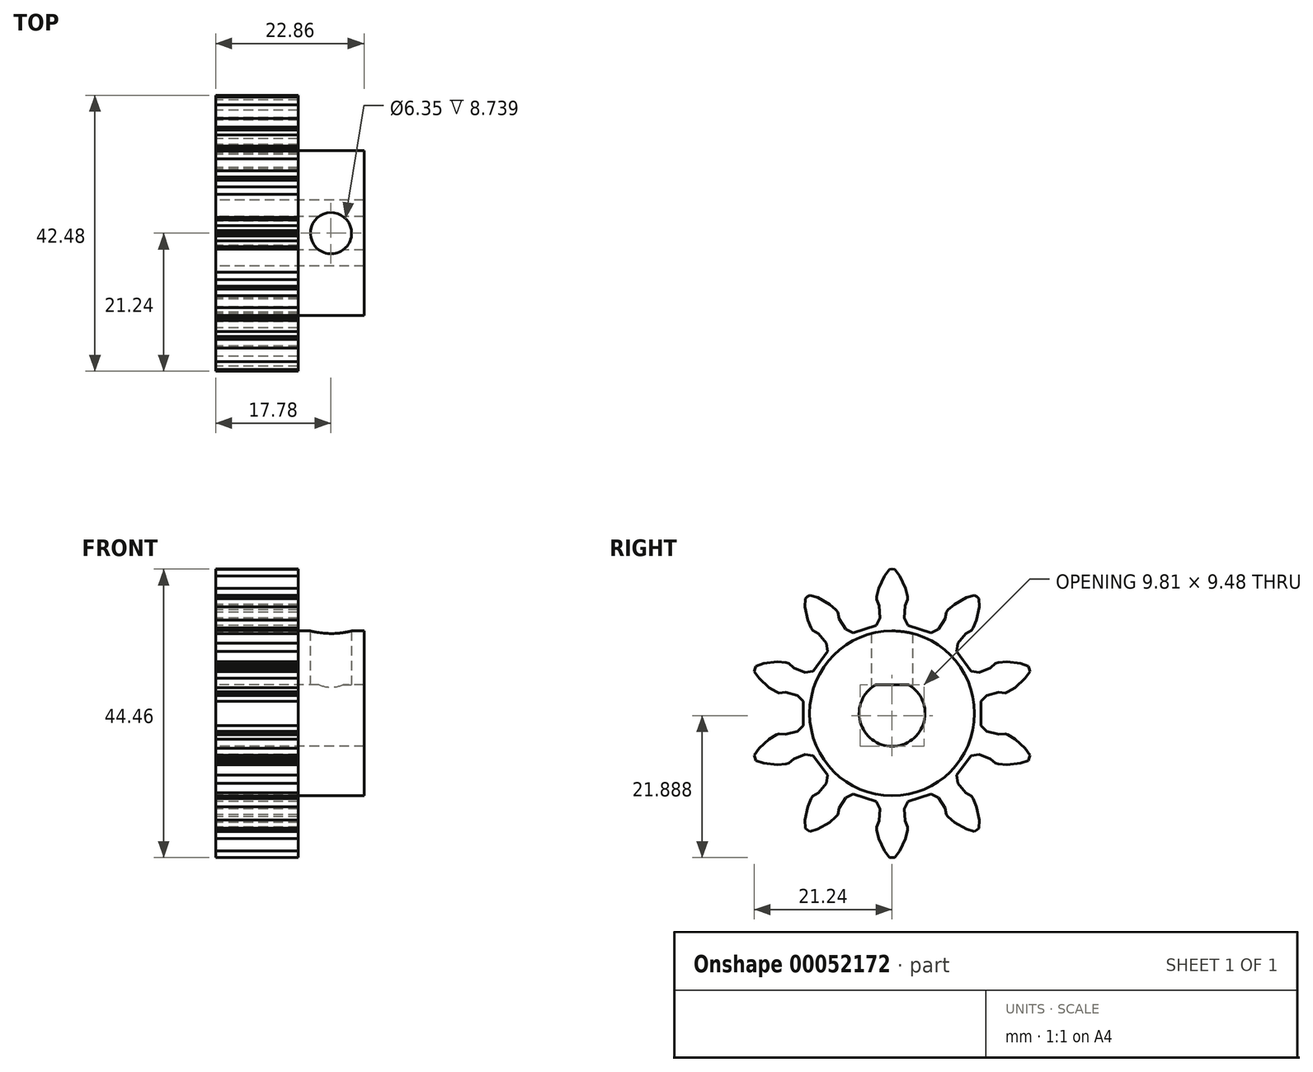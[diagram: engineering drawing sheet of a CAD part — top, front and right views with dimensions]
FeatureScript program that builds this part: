
annotation { "Feature Type Name" : "Feature", "Feature Type Description" : "" }
export const myFeature = defineFeature(function(context is Context, id is Id, definition is map)
    precondition{}
    {
        {
            var Q0;
            Q0=qCreatedBy(makeId("Right.planeOp"),FACE);
            var sketch = newSketch(context, id + "F0", { "sketchPlane" : qUnion([Q0])});
            skLineSegment(sketch, "E0", {"start": v(-20.97, 7.27) * mm, "end": v(-21.14, 6.87) * mm});
            skLineSegment(sketch, "E1", {"start": v(-21.14, 6.87) * mm, "end": v(-21.24, 6.44) * mm});
            skLineSegment(sketch, "E2", {"start": v(-21.24, 6.44) * mm, "end": v(-20.5, 5.4) * mm});
            skLineSegment(sketch, "E3", {"start": v(-20.5, 5.4) * mm, "end": v(-18.97, 3.97) * mm});
            skLineSegment(sketch, "E4", {"start": v(-18.97, 3.97) * mm, "end": v(-17.83, 3.3) * mm});
            skLineSegment(sketch, "E5", {"start": v(-17.83, 3.3) * mm, "end": v(-17.4, 3.15) * mm});
            skLineSegment(sketch, "E6", {"start": v(-17.4, 3.15) * mm, "end": v(-16.39, 3.24) * mm});
            skLineSegment(sketch, "E7", {"start": v(-16.39, 3.24) * mm, "end": v(-14.55, 2.78) * mm});
            skLineSegment(sketch, "E8", {"start": v(-14.55, 2.78) * mm, "end": v(-13.65, 1.86) * mm});
            skLineSegment(sketch, "E9", {"start": v(-13.65, 1.86) * mm, "end": v(-13.65, -1.86) * mm});
            skLineSegment(sketch, "E10", {"start": v(-13.65, -1.86) * mm, "end": v(-14.55, -2.78) * mm});
            skLineSegment(sketch, "E11", {"start": v(-14.55, -2.78) * mm, "end": v(-16.39, -3.24) * mm});
            skLineSegment(sketch, "E12", {"start": v(-16.39, -3.24) * mm, "end": v(-17.4, -3.15) * mm});
            skLineSegment(sketch, "E13", {"start": v(-17.4, -3.15) * mm, "end": v(-17.83, -3.3) * mm});
            skLineSegment(sketch, "E14", {"start": v(-17.83, -3.3) * mm, "end": v(-18.97, -3.97) * mm});
            skLineSegment(sketch, "E15", {"start": v(-18.97, -3.97) * mm, "end": v(-20.5, -5.4) * mm});
            skLineSegment(sketch, "E16", {"start": v(-20.5, -5.4) * mm, "end": v(-21.24, -6.44) * mm});
            skLineSegment(sketch, "E17", {"start": v(-21.24, -6.44) * mm, "end": v(-21.14, -6.87) * mm});
            skLineSegment(sketch, "E18", {"start": v(-21.14, -6.87) * mm, "end": v(-20.97, -7.27) * mm});
            skLineSegment(sketch, "E19", {"start": v(-20.97, -7.27) * mm, "end": v(-19.77, -7.68) * mm});
            skLineSegment(sketch, "E20", {"start": v(-19.77, -7.68) * mm, "end": v(-17.68, -7.93) * mm});
            skLineSegment(sketch, "E21", {"start": v(-17.68, -7.93) * mm, "end": v(-16.36, -7.82) * mm});
            skLineSegment(sketch, "E22", {"start": v(-16.36, -7.82) * mm, "end": v(-15.93, -7.68) * mm});
            skLineSegment(sketch, "E23", {"start": v(-15.93, -7.68) * mm, "end": v(-15.16, -7.01) * mm});
            skLineSegment(sketch, "E24", {"start": v(-15.16, -7.01) * mm, "end": v(-13.4, -6.3) * mm});
            skLineSegment(sketch, "E25", {"start": v(-13.4, -6.3) * mm, "end": v(-12.14, -6.52) * mm});
            skLineSegment(sketch, "E26", {"start": v(-12.14, -6.52) * mm, "end": v(-9.95, -9.53) * mm});
            skLineSegment(sketch, "E27", {"start": v(-9.95, -9.53) * mm, "end": v(-10.14, -10.8) * mm});
            skLineSegment(sketch, "E28", {"start": v(-10.14, -10.8) * mm, "end": v(-11.35, -12.25) * mm});
            skLineSegment(sketch, "E29", {"start": v(-11.35, -12.25) * mm, "end": v(-12.23, -12.77) * mm});
            skLineSegment(sketch, "E30", {"start": v(-12.23, -12.77) * mm, "end": v(-12.49, -13.14) * mm});
            skLineSegment(sketch, "E31", {"start": v(-12.49, -13.14) * mm, "end": v(-13, -14.36) * mm});
            skLineSegment(sketch, "E32", {"start": v(-13, -14.36) * mm, "end": v(-13.41, -16.43) * mm});
            skLineSegment(sketch, "E33", {"start": v(-13.41, -16.43) * mm, "end": v(-13.4, -17.7) * mm});
            skLineSegment(sketch, "E34", {"start": v(-13.4, -17.7) * mm, "end": v(-13.06, -17.98) * mm});
            skLineSegment(sketch, "E35", {"start": v(-13.06, -17.98) * mm, "end": v(-12.7, -18.2) * mm});
            skLineSegment(sketch, "E36", {"start": v(-12.7, -18.2) * mm, "end": v(-11.48, -17.83) * mm});
            skLineSegment(sketch, "E37", {"start": v(-11.48, -17.83) * mm, "end": v(-9.64, -16.81) * mm});
            skLineSegment(sketch, "E38", {"start": v(-9.64, -16.81) * mm, "end": v(-8.64, -15.94) * mm});
            skLineSegment(sketch, "E39", {"start": v(-8.64, -15.94) * mm, "end": v(-8.37, -15.58) * mm});
            skLineSegment(sketch, "E40", {"start": v(-8.37, -15.58) * mm, "end": v(-8.14, -14.58) * mm});
            skLineSegment(sketch, "E41", {"start": v(-8.14, -14.58) * mm, "end": v(-7.14, -12.98) * mm});
            skLineSegment(sketch, "E42", {"start": v(-7.14, -12.98) * mm, "end": v(-6, -12.4) * mm});
            skLineSegment(sketch, "E43", {"start": v(-6, -12.4) * mm, "end": v(-2.45, -13.56) * mm});
            skLineSegment(sketch, "E44", {"start": v(-2.45, -13.56) * mm, "end": v(-1.85, -14.7) * mm});
            skLineSegment(sketch, "E45", {"start": v(-1.85, -14.7) * mm, "end": v(-1.99, -16.58) * mm});
            skLineSegment(sketch, "E46", {"start": v(-1.99, -16.58) * mm, "end": v(-2.39, -17.52) * mm});
            skLineSegment(sketch, "E47", {"start": v(-2.39, -17.52) * mm, "end": v(-2.38, -17.97) * mm});
            skLineSegment(sketch, "E48", {"start": v(-2.38, -17.97) * mm, "end": v(-2.08, -19.27) * mm});
            skLineSegment(sketch, "E49", {"start": v(-2.08, -19.27) * mm, "end": v(-1.2, -21.17) * mm});
            skLineSegment(sketch, "E50", {"start": v(-1.2, -21.17) * mm, "end": v(-0.43, -22.2) * mm});
            skLineSegment(sketch, "E51", {"start": v(-0.43, -22.2) * mm, "end": v(0, -22.23) * mm});
            skLineSegment(sketch, "E52", {"start": v(0, -22.23) * mm, "end": v(0.43, -22.2) * mm});
            skLineSegment(sketch, "E53", {"start": v(0.43, -22.2) * mm, "end": v(1.2, -21.17) * mm});
            skLineSegment(sketch, "E54", {"start": v(1.2, -21.17) * mm, "end": v(2.08, -19.27) * mm});
            skLineSegment(sketch, "E55", {"start": v(2.08, -19.27) * mm, "end": v(2.38, -17.97) * mm});
            skLineSegment(sketch, "E56", {"start": v(2.38, -17.97) * mm, "end": v(2.39, -17.52) * mm});
            skLineSegment(sketch, "E57", {"start": v(2.39, -17.52) * mm, "end": v(1.99, -16.58) * mm});
            skLineSegment(sketch, "E58", {"start": v(1.99, -16.58) * mm, "end": v(1.85, -14.7) * mm});
            skLineSegment(sketch, "E59", {"start": v(1.85, -14.7) * mm, "end": v(2.45, -13.56) * mm});
            skLineSegment(sketch, "E60", {"start": v(2.45, -13.56) * mm, "end": v(6, -12.4) * mm});
            skLineSegment(sketch, "E61", {"start": v(6, -12.4) * mm, "end": v(7.14, -12.98) * mm});
            skLineSegment(sketch, "E62", {"start": v(7.14, -12.98) * mm, "end": v(8.14, -14.58) * mm});
            skLineSegment(sketch, "E63", {"start": v(8.14, -14.58) * mm, "end": v(8.37, -15.58) * mm});
            skLineSegment(sketch, "E64", {"start": v(8.37, -15.58) * mm, "end": v(8.64, -15.94) * mm});
            skLineSegment(sketch, "E65", {"start": v(8.64, -15.94) * mm, "end": v(9.64, -16.81) * mm});
            skLineSegment(sketch, "E66", {"start": v(9.64, -16.81) * mm, "end": v(11.48, -17.83) * mm});
            skLineSegment(sketch, "E67", {"start": v(11.48, -17.83) * mm, "end": v(12.7, -18.2) * mm});
            skLineSegment(sketch, "E68", {"start": v(12.7, -18.2) * mm, "end": v(13.06, -17.98) * mm});
            skLineSegment(sketch, "E69", {"start": v(13.06, -17.98) * mm, "end": v(13.4, -17.7) * mm});
            skLineSegment(sketch, "E70", {"start": v(13.4, -17.7) * mm, "end": v(13.41, -16.43) * mm});
            skLineSegment(sketch, "E71", {"start": v(13.41, -16.43) * mm, "end": v(13, -14.36) * mm});
            skLineSegment(sketch, "E72", {"start": v(13, -14.36) * mm, "end": v(12.49, -13.14) * mm});
            skLineSegment(sketch, "E73", {"start": v(12.49, -13.14) * mm, "end": v(12.23, -12.77) * mm});
            skLineSegment(sketch, "E74", {"start": v(12.23, -12.77) * mm, "end": v(11.35, -12.25) * mm});
            skLineSegment(sketch, "E75", {"start": v(11.35, -12.25) * mm, "end": v(10.14, -10.8) * mm});
            skLineSegment(sketch, "E76", {"start": v(10.14, -10.8) * mm, "end": v(9.95, -9.53) * mm});
            skLineSegment(sketch, "E77", {"start": v(9.95, -9.53) * mm, "end": v(12.14, -6.52) * mm});
            skLineSegment(sketch, "E78", {"start": v(12.14, -6.52) * mm, "end": v(13.4, -6.3) * mm});
            skLineSegment(sketch, "E79", {"start": v(13.4, -6.3) * mm, "end": v(15.16, -7.01) * mm});
            skLineSegment(sketch, "E80", {"start": v(15.16, -7.01) * mm, "end": v(15.93, -7.68) * mm});
            skLineSegment(sketch, "E81", {"start": v(15.93, -7.68) * mm, "end": v(16.36, -7.82) * mm});
            skLineSegment(sketch, "E82", {"start": v(16.36, -7.82) * mm, "end": v(17.68, -7.93) * mm});
            skLineSegment(sketch, "E83", {"start": v(17.68, -7.93) * mm, "end": v(19.77, -7.68) * mm});
            skLineSegment(sketch, "E84", {"start": v(19.77, -7.68) * mm, "end": v(20.97, -7.27) * mm});
            skLineSegment(sketch, "E85", {"start": v(20.97, -7.27) * mm, "end": v(21.14, -6.87) * mm});
            skLineSegment(sketch, "E86", {"start": v(21.14, -6.87) * mm, "end": v(21.24, -6.44) * mm});
            skLineSegment(sketch, "E87", {"start": v(21.24, -6.44) * mm, "end": v(20.5, -5.4) * mm});
            skLineSegment(sketch, "E88", {"start": v(20.5, -5.4) * mm, "end": v(18.97, -3.97) * mm});
            skLineSegment(sketch, "E89", {"start": v(18.97, -3.97) * mm, "end": v(17.83, -3.3) * mm});
            skLineSegment(sketch, "E90", {"start": v(17.83, -3.3) * mm, "end": v(17.4, -3.15) * mm});
            skLineSegment(sketch, "E91", {"start": v(17.4, -3.15) * mm, "end": v(16.39, -3.24) * mm});
            skLineSegment(sketch, "E92", {"start": v(16.39, -3.24) * mm, "end": v(14.55, -2.78) * mm});
            skLineSegment(sketch, "E93", {"start": v(14.55, -2.78) * mm, "end": v(13.65, -1.86) * mm});
            skLineSegment(sketch, "E94", {"start": v(13.65, -1.86) * mm, "end": v(13.65, 1.86) * mm});
            skLineSegment(sketch, "E95", {"start": v(13.65, 1.86) * mm, "end": v(14.55, 2.78) * mm});
            skLineSegment(sketch, "E96", {"start": v(14.55, 2.78) * mm, "end": v(16.39, 3.24) * mm});
            skLineSegment(sketch, "E97", {"start": v(16.39, 3.24) * mm, "end": v(17.4, 3.15) * mm});
            skLineSegment(sketch, "E98", {"start": v(17.4, 3.15) * mm, "end": v(17.83, 3.3) * mm});
            skLineSegment(sketch, "E99", {"start": v(17.83, 3.3) * mm, "end": v(18.97, 3.97) * mm});
            skLineSegment(sketch, "E100", {"start": v(18.97, 3.97) * mm, "end": v(20.5, 5.4) * mm});
            skLineSegment(sketch, "E101", {"start": v(20.5, 5.4) * mm, "end": v(21.24, 6.44) * mm});
            skLineSegment(sketch, "E102", {"start": v(21.24, 6.44) * mm, "end": v(21.14, 6.87) * mm});
            skLineSegment(sketch, "E103", {"start": v(21.14, 6.87) * mm, "end": v(20.97, 7.27) * mm});
            skLineSegment(sketch, "E104", {"start": v(20.97, 7.27) * mm, "end": v(19.77, 7.68) * mm});
            skLineSegment(sketch, "E105", {"start": v(19.77, 7.68) * mm, "end": v(17.68, 7.93) * mm});
            skLineSegment(sketch, "E106", {"start": v(17.68, 7.93) * mm, "end": v(16.36, 7.82) * mm});
            skLineSegment(sketch, "E107", {"start": v(16.36, 7.82) * mm, "end": v(15.93, 7.68) * mm});
            skLineSegment(sketch, "E108", {"start": v(15.93, 7.68) * mm, "end": v(15.16, 7.01) * mm});
            skLineSegment(sketch, "E109", {"start": v(15.16, 7.01) * mm, "end": v(13.4, 6.3) * mm});
            skLineSegment(sketch, "E110", {"start": v(13.4, 6.3) * mm, "end": v(12.14, 6.52) * mm});
            skLineSegment(sketch, "E111", {"start": v(12.14, 6.52) * mm, "end": v(9.95, 9.53) * mm});
            skLineSegment(sketch, "E112", {"start": v(9.95, 9.53) * mm, "end": v(10.14, 10.8) * mm});
            skLineSegment(sketch, "E113", {"start": v(10.14, 10.8) * mm, "end": v(11.35, 12.25) * mm});
            skLineSegment(sketch, "E114", {"start": v(11.35, 12.25) * mm, "end": v(12.23, 12.77) * mm});
            skLineSegment(sketch, "E115", {"start": v(12.23, 12.77) * mm, "end": v(12.49, 13.14) * mm});
            skLineSegment(sketch, "E116", {"start": v(12.49, 13.14) * mm, "end": v(13, 14.36) * mm});
            skLineSegment(sketch, "E117", {"start": v(13, 14.36) * mm, "end": v(13.41, 16.43) * mm});
            skLineSegment(sketch, "E118", {"start": v(13.41, 16.43) * mm, "end": v(13.4, 17.7) * mm});
            skLineSegment(sketch, "E119", {"start": v(13.4, 17.7) * mm, "end": v(13.06, 17.98) * mm});
            skLineSegment(sketch, "E120", {"start": v(13.06, 17.98) * mm, "end": v(12.7, 18.2) * mm});
            skLineSegment(sketch, "E121", {"start": v(12.7, 18.2) * mm, "end": v(11.48, 17.83) * mm});
            skLineSegment(sketch, "E122", {"start": v(11.48, 17.83) * mm, "end": v(9.64, 16.81) * mm});
            skLineSegment(sketch, "E123", {"start": v(9.64, 16.81) * mm, "end": v(8.64, 15.94) * mm});
            skLineSegment(sketch, "E124", {"start": v(8.64, 15.94) * mm, "end": v(8.37, 15.58) * mm});
            skLineSegment(sketch, "E125", {"start": v(8.37, 15.58) * mm, "end": v(8.14, 14.58) * mm});
            skLineSegment(sketch, "E126", {"start": v(8.14, 14.58) * mm, "end": v(7.14, 12.98) * mm});
            skLineSegment(sketch, "E127", {"start": v(7.14, 12.98) * mm, "end": v(6, 12.4) * mm});
            skLineSegment(sketch, "E128", {"start": v(6, 12.4) * mm, "end": v(2.45, 13.56) * mm});
            skLineSegment(sketch, "E129", {"start": v(2.45, 13.56) * mm, "end": v(1.85, 14.7) * mm});
            skLineSegment(sketch, "E130", {"start": v(1.85, 14.7) * mm, "end": v(1.99, 16.58) * mm});
            skLineSegment(sketch, "E131", {"start": v(1.99, 16.58) * mm, "end": v(2.39, 17.52) * mm});
            skLineSegment(sketch, "E132", {"start": v(2.39, 17.52) * mm, "end": v(2.38, 17.97) * mm});
            skLineSegment(sketch, "E133", {"start": v(2.38, 17.97) * mm, "end": v(2.08, 19.27) * mm});
            skLineSegment(sketch, "E134", {"start": v(2.08, 19.27) * mm, "end": v(1.2, 21.17) * mm});
            skLineSegment(sketch, "E135", {"start": v(1.2, 21.17) * mm, "end": v(0.43, 22.2) * mm});
            skLineSegment(sketch, "E136", {"start": v(0.43, 22.2) * mm, "end": v(0, 22.23) * mm});
            skLineSegment(sketch, "E137", {"start": v(0, 22.23) * mm, "end": v(-0.43, 22.2) * mm});
            skLineSegment(sketch, "E138", {"start": v(-0.43, 22.2) * mm, "end": v(-1.2, 21.17) * mm});
            skLineSegment(sketch, "E139", {"start": v(-1.2, 21.17) * mm, "end": v(-2.08, 19.27) * mm});
            skLineSegment(sketch, "E140", {"start": v(-2.08, 19.27) * mm, "end": v(-2.38, 17.97) * mm});
            skLineSegment(sketch, "E141", {"start": v(-2.38, 17.97) * mm, "end": v(-2.39, 17.52) * mm});
            skLineSegment(sketch, "E142", {"start": v(-2.39, 17.52) * mm, "end": v(-1.99, 16.58) * mm});
            skLineSegment(sketch, "E143", {"start": v(-1.99, 16.58) * mm, "end": v(-1.85, 14.7) * mm});
            skLineSegment(sketch, "E144", {"start": v(-1.85, 14.7) * mm, "end": v(-2.45, 13.56) * mm});
            skLineSegment(sketch, "E145", {"start": v(-2.45, 13.56) * mm, "end": v(-6, 12.4) * mm});
            skLineSegment(sketch, "E146", {"start": v(-6, 12.4) * mm, "end": v(-7.14, 12.98) * mm});
            skLineSegment(sketch, "E147", {"start": v(-7.14, 12.98) * mm, "end": v(-8.14, 14.58) * mm});
            skLineSegment(sketch, "E148", {"start": v(-8.14, 14.58) * mm, "end": v(-8.37, 15.58) * mm});
            skLineSegment(sketch, "E149", {"start": v(-8.37, 15.58) * mm, "end": v(-8.64, 15.94) * mm});
            skLineSegment(sketch, "E150", {"start": v(-8.64, 15.94) * mm, "end": v(-9.64, 16.81) * mm});
            skLineSegment(sketch, "E151", {"start": v(-9.64, 16.81) * mm, "end": v(-11.48, 17.83) * mm});
            skLineSegment(sketch, "E152", {"start": v(-11.48, 17.83) * mm, "end": v(-12.7, 18.2) * mm});
            skLineSegment(sketch, "E153", {"start": v(-12.7, 18.2) * mm, "end": v(-13.06, 17.98) * mm});
            skLineSegment(sketch, "E154", {"start": v(-13.06, 17.98) * mm, "end": v(-13.4, 17.7) * mm});
            skLineSegment(sketch, "E155", {"start": v(-13.4, 17.7) * mm, "end": v(-13.41, 16.43) * mm});
            skLineSegment(sketch, "E156", {"start": v(-13.41, 16.43) * mm, "end": v(-13, 14.36) * mm});
            skLineSegment(sketch, "E157", {"start": v(-13, 14.36) * mm, "end": v(-12.49, 13.14) * mm});
            skLineSegment(sketch, "E158", {"start": v(-12.49, 13.14) * mm, "end": v(-12.23, 12.77) * mm});
            skLineSegment(sketch, "E159", {"start": v(-12.23, 12.77) * mm, "end": v(-11.35, 12.25) * mm});
            skLineSegment(sketch, "E160", {"start": v(-11.35, 12.25) * mm, "end": v(-10.14, 10.8) * mm});
            skLineSegment(sketch, "E161", {"start": v(-10.14, 10.8) * mm, "end": v(-9.95, 9.53) * mm});
            skLineSegment(sketch, "E162", {"start": v(-9.95, 9.53) * mm, "end": v(-12.14, 6.52) * mm});
            skLineSegment(sketch, "E163", {"start": v(-12.14, 6.52) * mm, "end": v(-13.4, 6.3) * mm});
            skLineSegment(sketch, "E164", {"start": v(-13.4, 6.3) * mm, "end": v(-15.16, 7.01) * mm});
            skLineSegment(sketch, "E165", {"start": v(-15.16, 7.01) * mm, "end": v(-15.93, 7.68) * mm});
            skLineSegment(sketch, "E166", {"start": v(-15.93, 7.68) * mm, "end": v(-16.36, 7.82) * mm});
            skLineSegment(sketch, "E167", {"start": v(-16.36, 7.82) * mm, "end": v(-17.68, 7.93) * mm});
            skLineSegment(sketch, "E168", {"start": v(-17.68, 7.93) * mm, "end": v(-19.77, 7.68) * mm});
            skLineSegment(sketch, "E169", {"start": v(-19.77, 7.68) * mm, "end": v(-20.97, 7.27) * mm});
            skArc(sketch, "E170", {"start": v(-2.55, 4.4) * mm, "mid": v(0, -5.08) * mm, "end": v(2.55, 4.4) * mm});
            skLineSegment(sketch, "E171", {"start": v(-2.55, 4.4) * mm, "end": v(2.55, 4.4) * mm});
            skSolve(sketch);
        }
        {
            var Q0;
            Q0=makeQuery(id+"F0.imprint","IMPRINT",FACE,{"disambiguationData":[TD([[makeQuery(id+"F0.imprint","IMPRINT",EDGE,{"derivedFrom":sQuery(id+"F0.wireOp",EDGE,"E0")}),1.0]])]});
            extrude(context, id + "F1", {"entities" : qUnion([Q0]), "endBound" : BoundingType.SYMMETRIC, "depth" : 12.7 * mm});
        }
        {
            var Q0;
            Q0=makeQuery(id+"F1.opExtrude","CAP_FACE",FACE,{"disambiguationData":[OSD([sQuery(id+"F0.wireOp",EDGE,"E0"),sQuery(id+"F0.wireOp",EDGE,"E1"),sQuery(id+"F0.wireOp",EDGE,"E2"),sQuery(id+"F0.wireOp",EDGE,"E3"),sQuery(id+"F0.wireOp",EDGE,"E4"),sQuery(id+"F0.wireOp",EDGE,"E5"),sQuery(id+"F0.wireOp",EDGE,"E6"),sQuery(id+"F0.wireOp",EDGE,"E7"),sQuery(id+"F0.wireOp",EDGE,"E8"),sQuery(id+"F0.wireOp",EDGE,"E9"),sQuery(id+"F0.wireOp",EDGE,"E10"),sQuery(id+"F0.wireOp",EDGE,"E11"),sQuery(id+"F0.wireOp",EDGE,"E12"),sQuery(id+"F0.wireOp",EDGE,"E13"),sQuery(id+"F0.wireOp",EDGE,"E14"),sQuery(id+"F0.wireOp",EDGE,"E15"),sQuery(id+"F0.wireOp",EDGE,"E16"),sQuery(id+"F0.wireOp",EDGE,"E17"),sQuery(id+"F0.wireOp",EDGE,"E18"),sQuery(id+"F0.wireOp",EDGE,"E19"),sQuery(id+"F0.wireOp",EDGE,"E20"),sQuery(id+"F0.wireOp",EDGE,"E21"),sQuery(id+"F0.wireOp",EDGE,"E22"),sQuery(id+"F0.wireOp",EDGE,"E23"),sQuery(id+"F0.wireOp",EDGE,"E24"),sQuery(id+"F0.wireOp",EDGE,"E25"),sQuery(id+"F0.wireOp",EDGE,"E26"),sQuery(id+"F0.wireOp",EDGE,"E27"),sQuery(id+"F0.wireOp",EDGE,"E28"),sQuery(id+"F0.wireOp",EDGE,"E29"),sQuery(id+"F0.wireOp",EDGE,"E30"),sQuery(id+"F0.wireOp",EDGE,"E31"),sQuery(id+"F0.wireOp",EDGE,"E32"),sQuery(id+"F0.wireOp",EDGE,"E33"),sQuery(id+"F0.wireOp",EDGE,"E34"),sQuery(id+"F0.wireOp",EDGE,"E35"),sQuery(id+"F0.wireOp",EDGE,"E36"),sQuery(id+"F0.wireOp",EDGE,"E37"),sQuery(id+"F0.wireOp",EDGE,"E38"),sQuery(id+"F0.wireOp",EDGE,"E39"),sQuery(id+"F0.wireOp",EDGE,"E40"),sQuery(id+"F0.wireOp",EDGE,"E41"),sQuery(id+"F0.wireOp",EDGE,"E42"),sQuery(id+"F0.wireOp",EDGE,"E43"),sQuery(id+"F0.wireOp",EDGE,"E44"),sQuery(id+"F0.wireOp",EDGE,"E45"),sQuery(id+"F0.wireOp",EDGE,"E46"),sQuery(id+"F0.wireOp",EDGE,"E47"),sQuery(id+"F0.wireOp",EDGE,"E48"),sQuery(id+"F0.wireOp",EDGE,"E49"),sQuery(id+"F0.wireOp",EDGE,"E50"),sQuery(id+"F0.wireOp",EDGE,"E51"),sQuery(id+"F0.wireOp",EDGE,"E52"),sQuery(id+"F0.wireOp",EDGE,"E53"),sQuery(id+"F0.wireOp",EDGE,"E54"),sQuery(id+"F0.wireOp",EDGE,"E55"),sQuery(id+"F0.wireOp",EDGE,"E56"),sQuery(id+"F0.wireOp",EDGE,"E57"),sQuery(id+"F0.wireOp",EDGE,"E58"),sQuery(id+"F0.wireOp",EDGE,"E59"),sQuery(id+"F0.wireOp",EDGE,"E60"),sQuery(id+"F0.wireOp",EDGE,"E61"),sQuery(id+"F0.wireOp",EDGE,"E62"),sQuery(id+"F0.wireOp",EDGE,"E63"),sQuery(id+"F0.wireOp",EDGE,"E64"),sQuery(id+"F0.wireOp",EDGE,"E65"),sQuery(id+"F0.wireOp",EDGE,"E66"),sQuery(id+"F0.wireOp",EDGE,"E67"),sQuery(id+"F0.wireOp",EDGE,"E68"),sQuery(id+"F0.wireOp",EDGE,"E69"),sQuery(id+"F0.wireOp",EDGE,"E70"),sQuery(id+"F0.wireOp",EDGE,"E71"),sQuery(id+"F0.wireOp",EDGE,"E72"),sQuery(id+"F0.wireOp",EDGE,"E73"),sQuery(id+"F0.wireOp",EDGE,"E74"),sQuery(id+"F0.wireOp",EDGE,"E75"),sQuery(id+"F0.wireOp",EDGE,"E76"),sQuery(id+"F0.wireOp",EDGE,"E77"),sQuery(id+"F0.wireOp",EDGE,"E78"),sQuery(id+"F0.wireOp",EDGE,"E79"),sQuery(id+"F0.wireOp",EDGE,"E80"),sQuery(id+"F0.wireOp",EDGE,"E81"),sQuery(id+"F0.wireOp",EDGE,"E82"),sQuery(id+"F0.wireOp",EDGE,"E83"),sQuery(id+"F0.wireOp",EDGE,"E84"),sQuery(id+"F0.wireOp",EDGE,"E85"),sQuery(id+"F0.wireOp",EDGE,"E86"),sQuery(id+"F0.wireOp",EDGE,"E87"),sQuery(id+"F0.wireOp",EDGE,"E88"),sQuery(id+"F0.wireOp",EDGE,"E89"),sQuery(id+"F0.wireOp",EDGE,"E90"),sQuery(id+"F0.wireOp",EDGE,"E91"),sQuery(id+"F0.wireOp",EDGE,"E92"),sQuery(id+"F0.wireOp",EDGE,"E93"),sQuery(id+"F0.wireOp",EDGE,"E94"),sQuery(id+"F0.wireOp",EDGE,"E95"),sQuery(id+"F0.wireOp",EDGE,"E96"),sQuery(id+"F0.wireOp",EDGE,"E97"),sQuery(id+"F0.wireOp",EDGE,"E98"),sQuery(id+"F0.wireOp",EDGE,"E99"),sQuery(id+"F0.wireOp",EDGE,"E100"),sQuery(id+"F0.wireOp",EDGE,"E101"),sQuery(id+"F0.wireOp",EDGE,"E102"),sQuery(id+"F0.wireOp",EDGE,"E103"),sQuery(id+"F0.wireOp",EDGE,"E104"),sQuery(id+"F0.wireOp",EDGE,"E105"),sQuery(id+"F0.wireOp",EDGE,"E106"),sQuery(id+"F0.wireOp",EDGE,"E107"),sQuery(id+"F0.wireOp",EDGE,"E108"),sQuery(id+"F0.wireOp",EDGE,"E109"),sQuery(id+"F0.wireOp",EDGE,"E110"),sQuery(id+"F0.wireOp",EDGE,"E111"),sQuery(id+"F0.wireOp",EDGE,"E112"),sQuery(id+"F0.wireOp",EDGE,"E113"),sQuery(id+"F0.wireOp",EDGE,"E114"),sQuery(id+"F0.wireOp",EDGE,"E115"),sQuery(id+"F0.wireOp",EDGE,"E116"),sQuery(id+"F0.wireOp",EDGE,"E117"),sQuery(id+"F0.wireOp",EDGE,"E118"),sQuery(id+"F0.wireOp",EDGE,"E119"),sQuery(id+"F0.wireOp",EDGE,"E120"),sQuery(id+"F0.wireOp",EDGE,"E121"),sQuery(id+"F0.wireOp",EDGE,"E122"),sQuery(id+"F0.wireOp",EDGE,"E123"),sQuery(id+"F0.wireOp",EDGE,"E124"),sQuery(id+"F0.wireOp",EDGE,"E125"),sQuery(id+"F0.wireOp",EDGE,"E126"),sQuery(id+"F0.wireOp",EDGE,"E127"),sQuery(id+"F0.wireOp",EDGE,"E128"),sQuery(id+"F0.wireOp",EDGE,"E129"),sQuery(id+"F0.wireOp",EDGE,"E130"),sQuery(id+"F0.wireOp",EDGE,"E131"),sQuery(id+"F0.wireOp",EDGE,"E132"),sQuery(id+"F0.wireOp",EDGE,"E133"),sQuery(id+"F0.wireOp",EDGE,"E134"),sQuery(id+"F0.wireOp",EDGE,"E135"),sQuery(id+"F0.wireOp",EDGE,"E136"),sQuery(id+"F0.wireOp",EDGE,"E137"),sQuery(id+"F0.wireOp",EDGE,"E138"),sQuery(id+"F0.wireOp",EDGE,"E139"),sQuery(id+"F0.wireOp",EDGE,"E140"),sQuery(id+"F0.wireOp",EDGE,"E141"),sQuery(id+"F0.wireOp",EDGE,"E142"),sQuery(id+"F0.wireOp",EDGE,"E143"),sQuery(id+"F0.wireOp",EDGE,"E144"),sQuery(id+"F0.wireOp",EDGE,"E145"),sQuery(id+"F0.wireOp",EDGE,"E146"),sQuery(id+"F0.wireOp",EDGE,"E147"),sQuery(id+"F0.wireOp",EDGE,"E148"),sQuery(id+"F0.wireOp",EDGE,"E149"),sQuery(id+"F0.wireOp",EDGE,"E150"),sQuery(id+"F0.wireOp",EDGE,"E151"),sQuery(id+"F0.wireOp",EDGE,"E152"),sQuery(id+"F0.wireOp",EDGE,"E153"),sQuery(id+"F0.wireOp",EDGE,"E154"),sQuery(id+"F0.wireOp",EDGE,"E155"),sQuery(id+"F0.wireOp",EDGE,"E156"),sQuery(id+"F0.wireOp",EDGE,"E157"),sQuery(id+"F0.wireOp",EDGE,"E158"),sQuery(id+"F0.wireOp",EDGE,"E159"),sQuery(id+"F0.wireOp",EDGE,"E160"),sQuery(id+"F0.wireOp",EDGE,"E161"),sQuery(id+"F0.wireOp",EDGE,"E162"),sQuery(id+"F0.wireOp",EDGE,"E163"),sQuery(id+"F0.wireOp",EDGE,"E164"),sQuery(id+"F0.wireOp",EDGE,"E165"),sQuery(id+"F0.wireOp",EDGE,"E166"),sQuery(id+"F0.wireOp",EDGE,"E167"),sQuery(id+"F0.wireOp",EDGE,"E168"),sQuery(id+"F0.wireOp",EDGE,"E169"),sQuery(id+"F0.wireOp",EDGE,"E170"),sQuery(id+"F0.wireOp",EDGE,"E171")])],"isStart":false});
            var sketch = newSketch(context, id + "F2", { "sketchPlane" : qUnion([Q0])});
            skCircle(sketch, "E172", {"center": v(0, 0) * mm, "radius": 12.7 * mm});
            skArc(sketch, "E173", {"start": v(-2.55, 4.4) * mm, "mid": v(0, -5.08) * mm, "end": v(2.55, 4.4) * mm});
            skLineSegment(sketch, "E174", {"start": v(-2.55, 4.4) * mm, "end": v(2.55, 4.4) * mm});
            skSolve(sketch);
        }
        {
            var Q0;
            Q0=qSketchRegion(id+"F2",true);
            extrude(context, id + "F3", {"entities" : qUnion([Q0]), "operationType" : NewBodyOperationType.ADD, "depth" : 10.16 * mm});
        }
        {
            var Q0;
            Q0=qCreatedBy(makeId("Top.planeOp"),FACE);
            var sketch = newSketch(context, id + "F4", { "sketchPlane" : qUnion([Q0])});
            skCircle(sketch, "E175", {"center": v(11.43, 0) * mm, "radius": 3.18 * mm});
            skSolve(sketch);
        }
        {
            var Q0;
            Q0 = qSketchRegion(id + "F4", true);
            extrude(context, id + "F5", {"entities" : qUnion([Q0]), "operationType" : NewBodyOperationType.REMOVE, "depth" : 25.4 * mm});
        }
    });
